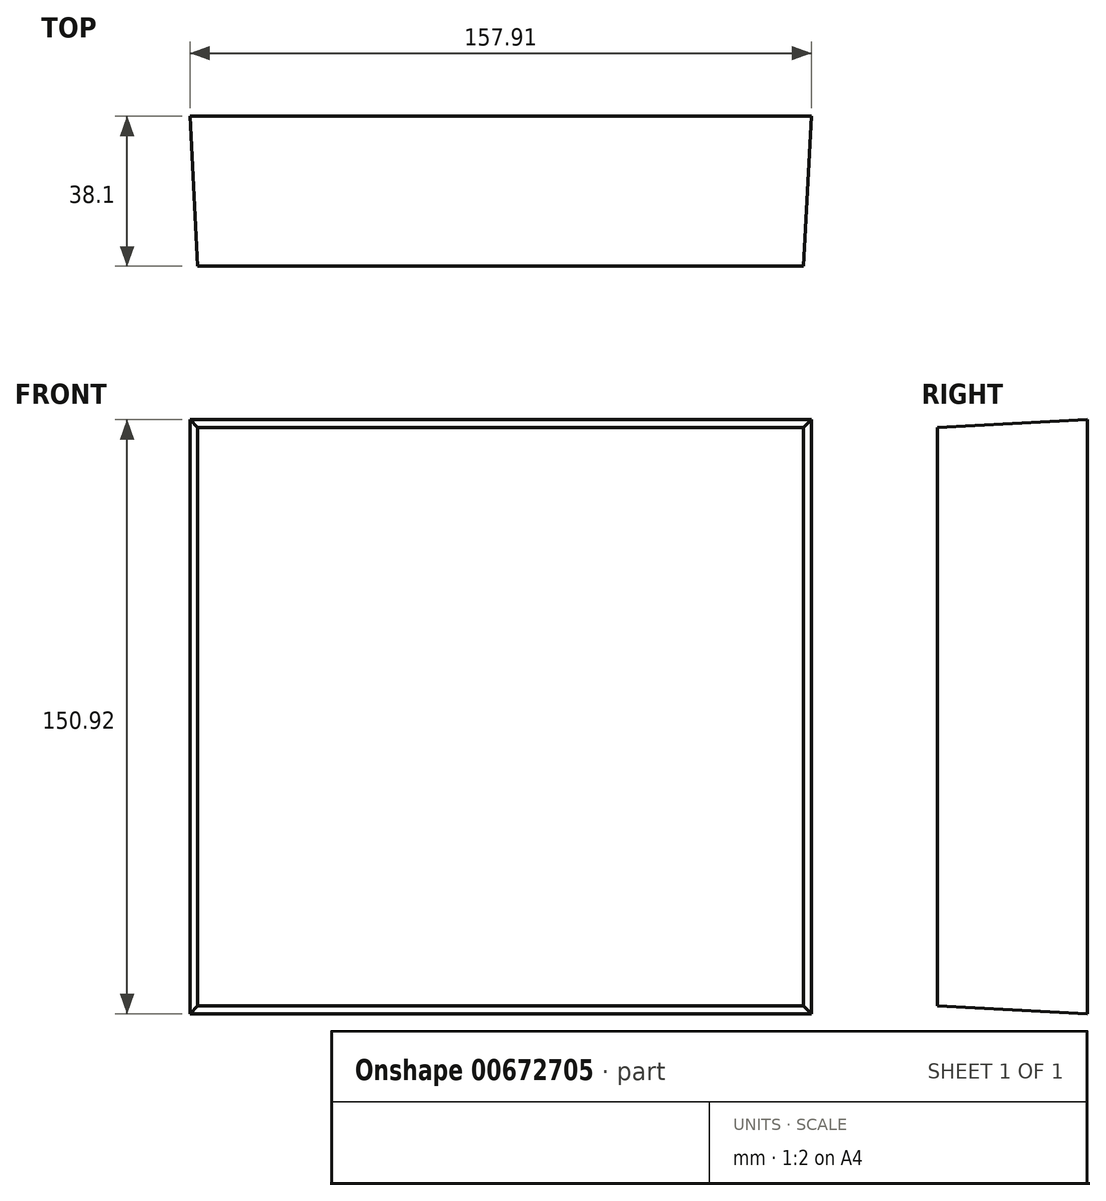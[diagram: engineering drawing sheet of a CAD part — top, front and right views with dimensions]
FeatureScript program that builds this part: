
annotation { "Feature Type Name" : "Feature", "Feature Type Description" : "" }
export const myFeature = defineFeature(function(context is Context, id is Id, definition is map)
    precondition{}
    {
        {
            var Q0;
            Q0=qCreatedBy(makeId("Front.planeOp"),FACE);
            var sketch = newSketch(context, id + "F0", { "sketchPlane" : qUnion([Q0])});
            skLineSegment(sketch, "E0.bottom", {"start": v(-74.24, 74.55) * mm, "end": v(79.69, 74.55) * mm});
            skLineSegment(sketch, "E0.top", {"start": v(-74.24, -72.38) * mm, "end": v(79.69, -72.38) * mm});
            skLineSegment(sketch, "E0.left", {"start": v(-74.24, 74.55) * mm, "end": v(-74.24, -72.38) * mm});
            skLineSegment(sketch, "E0.right", {"start": v(79.69, 74.55) * mm, "end": v(79.69, -72.38) * mm});
            skSolve(sketch);
        }
        {
            var Q0;
            Q0 = qSketchRegion(id + "F0", true);
            var sketch = newSketch(context, id + "F1", { "sketchPlane" : qUnion([Q0])});
            skSolve(sketch);
        }
        {
            var Q0;
            Q0 = qSketchRegion(id + "F0", true);
            extrude(context, id + "F2", {"entities" : qUnion([Q0]), "oppositeDirection" : true, "depth" : 38.1 * mm, "offsetDistance" : 25.4 * mm, "hasDraft" : true, "draftAngle" : 3 * degree});
        }
    });
